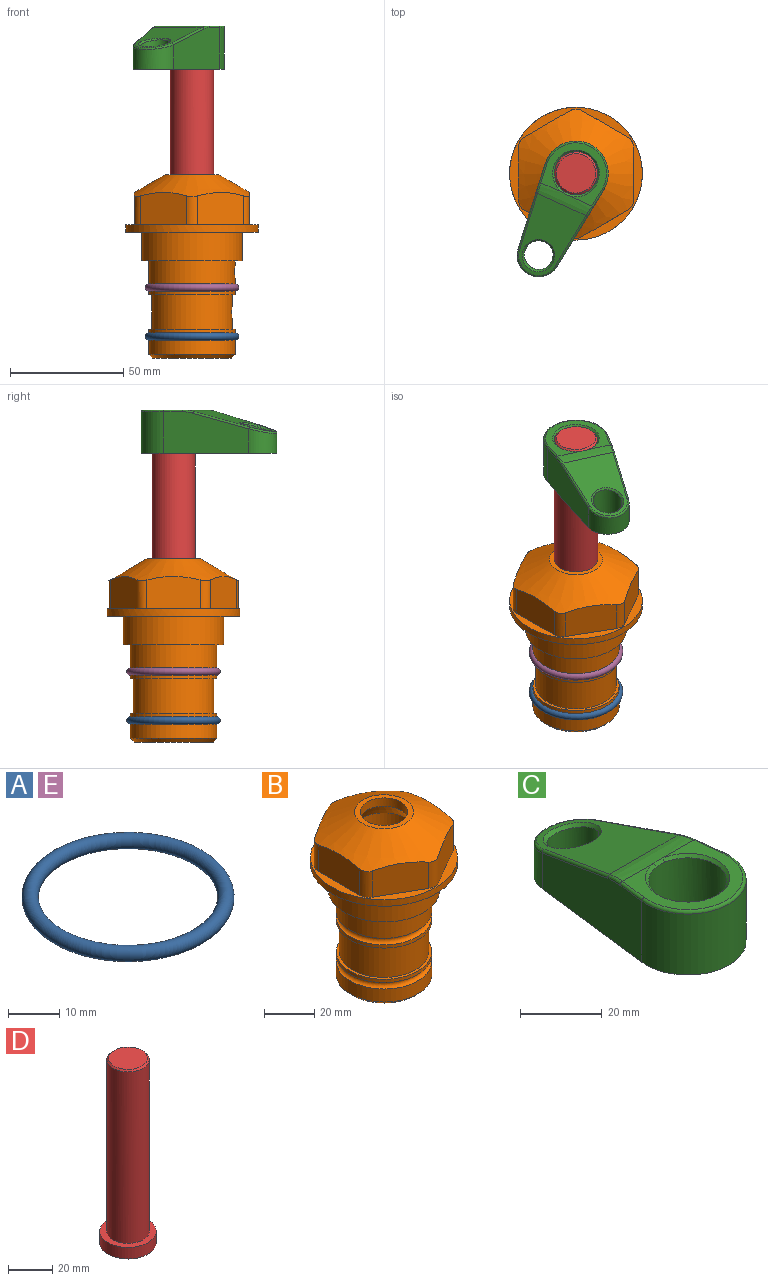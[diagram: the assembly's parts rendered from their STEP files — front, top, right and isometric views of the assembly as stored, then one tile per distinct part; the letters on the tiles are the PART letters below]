
ASSEMBLY  parts=5 mates=4
PART A: 1 faces, bbox 44.7x44.7x3.2 mm
  f0: torus R=19.05mm, axis (0,0,1), area 1193.9mm2
PART B: 36 faces, bbox 58.7x58.7x81 mm
  f0: cylinder r=17.78mm len=35.56mm, axis (0,0,1), area 1670.8mm2, adj f23,f24,f31
  f1: cylinder r=19.05mm len=38.1mm, axis (0,0,1), area 1191.9mm2, adj f26,f27,f30
  f2: plane 58.66x58.66mm, normal (0,0,-1), area 1150.6mm2, adj f3,f28
  f3: cylinder r=29.33mm len=58.66mm, axis (0,0,-1), area 585.1mm2, adj f2,f4
  f4: plane 58.66x58.66mm, normal (0,0,1), area 475.9mm2, adj f3,f5,f6,f7,f8,f9,f10,f11
  f5: plane 20.32x14.34mm, normal (-0.5,0.87,0), area 324.4mm2, adj f4,f15,f16,f17
  f6: plane 20.32x14.34mm, normal (0.5,0.87,0), area 324.4mm2, adj f4,f14,f15,f17
  f7: plane 23.48x14.34mm, normal (1,0,0), area 324.4mm2, adj f4,f13,f14,f17
  f8: plane 20.32x14.34mm, normal (0.5,-0.87,0), area 324.4mm2, adj f4,f12,f13,f17
  f9: plane 20.32x14.34mm, normal (-0.5,-0.87,0), area 324.4mm2, adj f4,f11,f12,f17
  f10: plane 23.48x14.34mm, normal (-1,0,0), area 324.4mm2, adj f4,f11,f16,f17
  f11: cylinder r=5.08mm len=12.85mm, axis (0,0,-1), area 67.2mm2, adj f4,f9,f10,f17
  f12: cylinder r=5.08mm len=12.85mm, axis (0,0,-1), area 67.2mm2, adj f4,f8,f9,f17
  f13: cylinder r=5.08mm len=12.85mm, axis (0,0,-1), area 67.2mm2, adj f4,f7,f8,f17
  f14: cylinder r=5.08mm len=12.85mm, axis (0,0,-1), area 67.2mm2, adj f4,f6,f7,f17
  f15: cylinder r=5.08mm len=12.85mm, axis (0,0,-1), area 67.2mm2, adj f4,f5,f6,f17
  f16: cylinder r=5.08mm len=12.85mm, axis (0,0,-1), area 67.2mm2, adj f4,f5,f10,f17
  f17: cone r=11.73mm half-angle=60deg, axis (0,0,-1), area 2071.8mm2, adj f5,f6,f7,f8,f9,f10,f11,f12
  f18: plane 23.46x23.46mm, normal (0,0,1), area 147.4mm2, adj f17,f35
  f19: plane 34.93x34.93mm, normal (0,0,-1), area 958mm2, adj f29
  f20: cylinder r=19.05mm len=38.1mm, axis (0,0,1), area 760.1mm2, adj f21,f29
  f21: torus R=19.05mm, axis (0,0,1), area 565.3mm2, adj f20,f22
  f22: cylinder r=19.05mm len=38.1mm, axis (0,0,1), area 190mm2, adj f21,f23
  f23: plane 38.1x38.1mm, normal (0,0,1), area 146.9mm2, adj f0,f22
  f24: plane 38.1x38.1mm, normal (0,0,-1), area 146.9mm2, adj f0,f25
  f25: cylinder r=19.05mm len=38.1mm, axis (0,0,1), area 190mm2, adj f24,f26
  f26: torus R=19.05mm, axis (0,0,1), area 565.3mm2, adj f1,f25
  f27: plane 44.45x44.45mm, normal (0,0,-1), area 411.7mm2, adj f1,f28
  f28: cylinder r=22.23mm len=44.45mm, axis (0,0,1), area 1773.5mm2, adj f2,f27
  f29: cone r=19.05mm half-angle=45deg, axis (0,0,1), area 257.5mm2, adj f19,f20
  f30: cylinder r=3.17mm len=6.75mm, axis (-1,0,0), area 128mm2, adj f1,f33
  f31: cylinder r=3.17mm len=6.35mm, axis (-1,0,0), area 102.5mm2, adj f0,f33
  f32: plane 25.4x25.4mm, normal (0,0,1), area 506.7mm2, adj f33
  f33: cylinder r=12.7mm len=66.42mm, axis (0,0,-1), area 5236.2mm2, adj f30,f31,f32,f34
  f34: cone r=9.53mm half-angle=30deg, axis (0,0,-1), area 443.4mm2, adj f33,f35
  f35: cylinder r=9.53mm len=19.05mm, axis (0,0,-1), area 240.9mm2, adj f18,f34
PART C: 31 faces, bbox 31.7x65.5x19.8 mm
  f0: plane 39.12x18.26mm, normal (0.99,0.12,0), area 612.2mm2, adj f1,f4,f7,f11,f13,f15
  f1: cylinder r=9.53mm len=18.91mm, axis (0,0,-1), area 296.1mm2, adj f0,f2,f7,f17
  f2: plane 39.12x18.26mm, normal (-0.99,0.12,0), area 612.2mm2, adj f1,f4,f7,f12,f14,f16
  f3: cylinder r=6.35mm len=12.7mm, axis (0,0,-1), area 362.4mm2, adj f7,f18
  f4: cylinder r=14.29mm len=28.58mm, axis (0,0,-1), area 882.2mm2, adj f0,f2,f7,f10
  f5: cylinder r=9.53mm len=19.05mm, axis (0,0,-1), area 1092.6mm2, adj f7,f19,f20
  f6: plane 26.99x23.69mm, normal (0,0,1), area 216.2mm2, adj f9,f10,f11,f12,f19
  f7: plane 63.5x28.58mm, normal (0,0,-1), area 661.8mm2, adj f0,f1,f2,f3,f4,f5,f22,f23
  f8: plane 33.52x23.6mm, normal (0,0.26,0.97), area 486mm2, adj f9,f15,f16,f17,f18
  f9: cylinder r=19.05mm len=24.72mm, axis (1,0,0), area 120.4mm2, adj f6,f8,f13,f14,f20
  f10: torus R=13.49mm, axis (0,0,1), area 59mm2, adj f4,f6,f11,f12
  f11: cylinder r=0.79mm len=8.67mm, axis (0.12,-0.99,0), area 10.8mm2, adj f0,f6,f10,f13
  f12: cylinder r=0.79mm len=8.67mm, axis (0.12,0.99,0), area 10.8mm2, adj f2,f6,f10,f14
  f13: bspline ~4.95x1.42mm, area 6.1mm2, adj f0,f9,f11,f15
  f14: bspline ~4.95x1.42mm, area 6.1mm2, adj f2,f9,f12,f16
  f15: cylinder r=0.79mm len=25.95mm, axis (0.12,-0.96,0.26), area 32.9mm2, adj f0,f8,f13,f17
  f16: cylinder r=0.79mm len=25.95mm, axis (0.12,0.96,-0.26), area 32.9mm2, adj f2,f8,f14,f17
  f17: bspline ~18.91x8.38mm, area 30mm2, adj f1,f8,f15,f16
  f18: bspline ~14.29x14.29mm, area 48.3mm2, adj f3,f8
  f19: cone r=9.53mm half-angle=45deg, axis (0,0,1), area 66.5mm2, adj f5,f6,f20
  f20: bspline ~3.22x0.96mm, area 3.5mm2, adj f5,f9,f19
  f21: plane 2.75x2.72mm, normal (0,0,-1), area 2.9mm2, adj f23,f25,f28
  f22: plane 23.05x15.88mm, normal (-0.99,-0.12,0), area 323.6mm2, adj f7,f25,f26,f27,f28,f29
  f23: plane 23.05x15.88mm, normal (0.99,-0.12,0), area 323.6mm2, adj f7,f21,f25,f27,f28,f30
  f24: cylinder r=9.53mm len=10.69mm, axis (0,0,-1), area 114.7mm2, adj f7,f27,f29,f30
  f25: cylinder r=12.7mm len=20.59mm, axis (0,0,-1), area 381.1mm2, adj f7,f21,f22,f23,f26,f28
  f26: plane 2.75x2.72mm, normal (0,0,-1), area 2.9mm2, adj f22,f25,f28
  f27: plane 19.72x18.37mm, normal (0,-0.26,-0.97), area 291.8mm2, adj f22,f23,f24,f28,f29,f30
  f28: cylinder r=15.88mm len=19.92mm, axis (1,0,0), area 54.8mm2, adj f21,f22,f23,f25,f26,f27
  f29: cylinder r=1.59mm len=11mm, axis (0,0,-1), area 34.7mm2, adj f7,f22,f24,f27
  f30: cylinder r=1.59mm len=11mm, axis (0,0,-1), area 34.7mm2, adj f7,f23,f24,f27
PART D: 6 faces, bbox 25.4x25.4x101.6 mm
  f0: plane 17.46x17.46mm, normal (0,0,1), area 239.5mm2, adj f5
  f1: plane 25.4x25.4mm, normal (0,0,-1), area 506.7mm2, adj f2
  f2: cylinder r=12.7mm len=25.4mm, axis (0,0,1), area 506.7mm2, adj f1,f3
  f3: plane 25.4x25.4mm, normal (0,0,1), area 221.7mm2, adj f2,f4
  f4: cylinder r=9.53mm len=94.46mm, axis (0,0,1), area 5653mm2, adj f3,f5
  f5: cone r=8.73mm half-angle=45deg, axis (0,0,-1), area 64.4mm2, adj f0,f4
PART E: same geometry as A
PLACE A t=(0,0,-21.59)mm
PLACE B at identity fixed
PLACE C rot(axis=(0,0,1),155.5deg) t=(0,0,27.55)mm
PLACE D rot(axis=(0,0,1),155.5deg) t=(0,0,27.55)mm
PLACE E at identity
MATE fastened A.f0 <-> B.f0  axis (0,0,1) through (0,0,-46.1)mm
MATE fastened C.f4 <-> D.f2  axis (0,0,-1) through (0,0,90.26)mm
MATE cylindrical B.f0 <-> D.f2  axis (0,0,1) through (0,0,-50.55)mm
MATE fastened B.f0 <-> E.f0  axis (0,0,1) through (0,0,-24.51)mm
